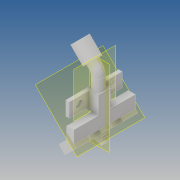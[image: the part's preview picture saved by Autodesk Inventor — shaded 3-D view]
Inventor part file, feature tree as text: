
AUTODESK INVENTOR PART (.ipt)
format: ipt  version: 2020 (Build 240168000, 168)  size: 558,592 bytes
history: native  units: mm
features: sketch x17, extrude x15, other x7, projected_geometry x4, revolve x1, chamfer x1
ambient origin geometry x8: Origin, YZ Plane, XZ Plane, XY Plane, X Axis, Y Axis, Z Axis, Center Point
bodies: Body1 (feature_tree)
feature tree (45):
  other  "솔리드1"
  extrude  "돌출1"  Depth=7.0mm
  extrude  "돌출2"  Depth=7.0mm
  extrude  "돌출3"  Depth=10.0mm TaperAngle=0.0deg
  other  "작업 평면1"
  revolve  "회전2"
  extrude  "돌출4"  Depth=6.0mm
  extrude  "돌출5"  Depth=13.0mm TaperAngle=0.0deg
  other  "작업 평면2"
  extrude  "돌출6"  Depth=9.0mm
  extrude  "돌출7"  Depth=10.0mm TaperAngle=0.0deg
  extrude  "돌출8"  Depth=2.75mm
  extrude  "돌출9"  Depth=5.0mm
  extrude  "돌출10"  Depth=2.5mm
  other  "작업 평면3"
  chamfer  "모따기1"  Distance=0.5mm
  extrude  "돌출12"  Depth=35.0mm
  extrude  "돌출13"  Depth=7.0mm
  extrude  "돌출14"  Depth=4.0mm TaperAngle=0.0deg
  extrude  "돌출15"  Depth=5.0mm
  extrude  "돌출16"  Depth=11.0mm TaperAngle=0.0deg
  other  "굽힘1"
  sketch  "스케치1"
  sketch  "스케치2"
  sketch  "스케치3"
  sketch  "스케치4"
  projected_geometry  "투영된 루프1"
  sketch  "스케치5"
  sketch  "스케치6"
  sketch  "스케치7"
  projected_geometry  "투영된 루프2"
  sketch  "스케치8"
  sketch  "스케치9"
  sketch  "스케치10"
  sketch  "스케치11"
  sketch  "스케치13"
  sketch  "스케치14"
  sketch  "스케치15"
  sketch  "스케치16"
  sketch  "스케치17"
  projected_geometry  "투영된 루프3"
  projected_geometry  "투영된 루프4"
  sketch  "스케치20"
  other  "절단 모서리 투영1"
  other  "절단 모서리 투영2"
